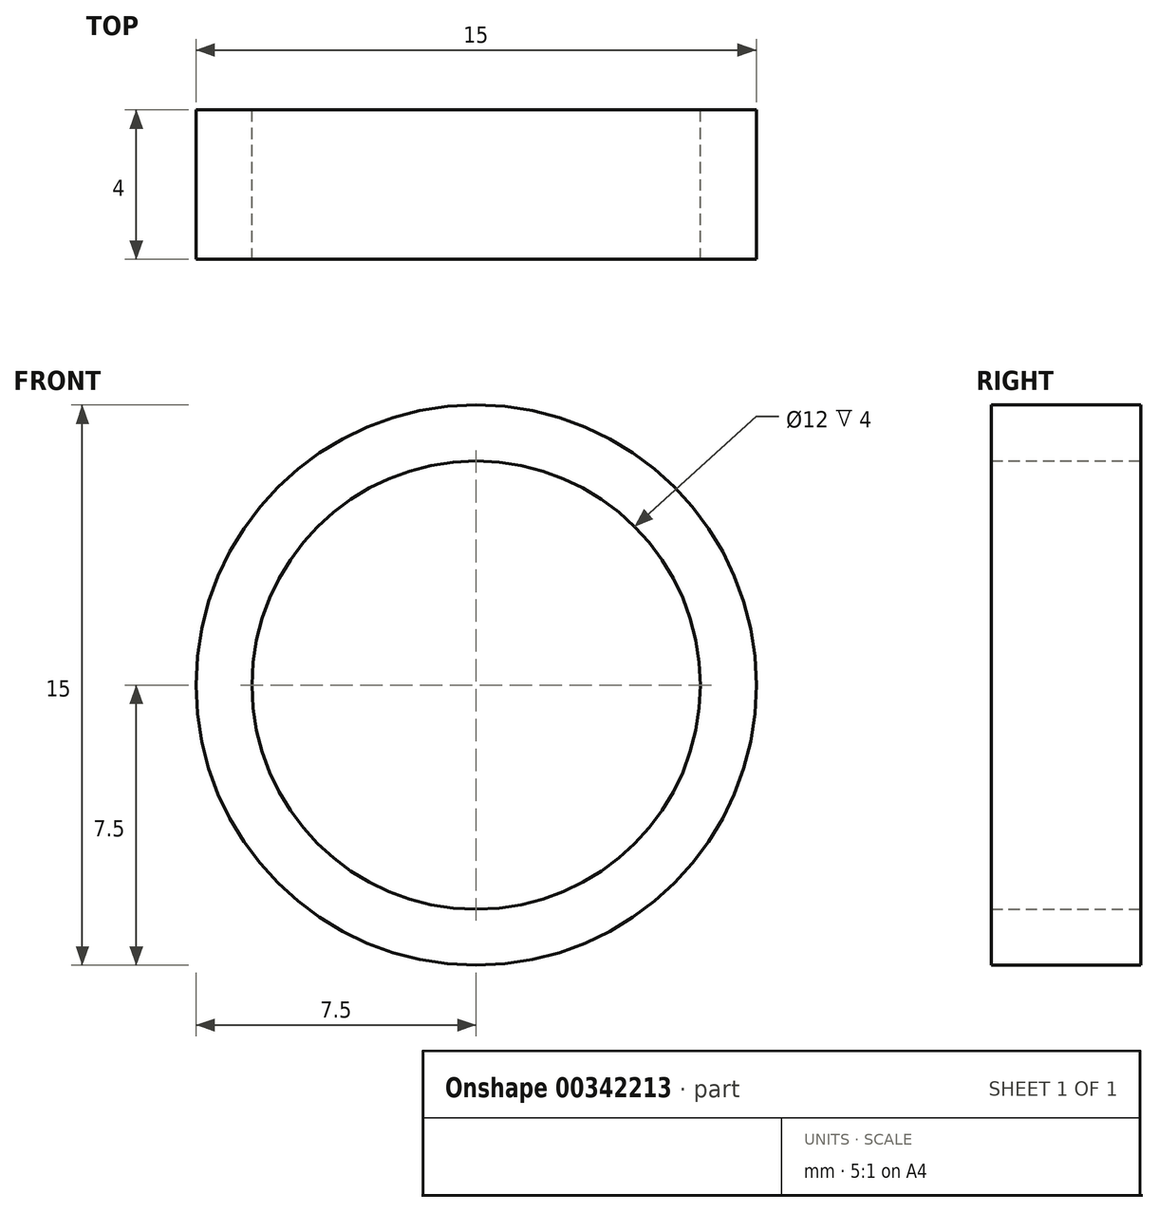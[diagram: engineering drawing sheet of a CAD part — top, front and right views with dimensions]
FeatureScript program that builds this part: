
annotation { "Feature Type Name" : "Feature", "Feature Type Description" : "" }
export const myFeature = defineFeature(function(context is Context, id is Id, definition is map)
    precondition{}
    {
        {
            var Q0;
            Q0=qCreatedBy(makeId("Front.planeOp"),FACE);
            var sketch = newSketch(context, id + "F0", { "sketchPlane" : qUnion([Q0])});
            skCircle(sketch, "E0", {"center": v(0, 0) * mm, "radius": 7.5 * mm});
            skCircle(sketch, "E1", {"center": v(0, 0) * mm, "radius": 6 * mm});
            skSolve(sketch);
        }
        {
            var Q0;
            Q0=makeQuery(id+"F0.imprint","IMPRINT",FACE,{"disambiguationData":[TD([[makeQuery(id+"F0.imprint","IMPRINT",EDGE,{"derivedFrom":sQuery(id+"F0.wireOp",EDGE,"E0")}),1.0]])]});
            extrude(context, id + "F1", {"entities" : qUnion([Q0]), "depth" : 4 * mm});
        }
    });
